# Revit family: Gira_028226
name_source: partatom
category: Electrical Fixtures
revit_build: Autodesk Revit 2017 (Build: 20160225_1515(x64)
units: mm (PartAtom-declared; Revit-internal decimal feet)

## family parameters
Cut with Voids When Loaded = No
Host = Face
Maintain Annotation Orientation = No
Part Type = Normal
Room Calculation Point = No
Round Connector Dimension = Use Diameter
Shared = No

## types (1)
- Adapter fr. square 50 x 50 mm System 55 c.alum.
    Available = No
    BIM (1) = https://media.stage.bim.site
    Category = Transition adapter for domestic switching devices
    Data sheet (1) = https://katalog.gira.de
    Default Elevation = 1219 mm
    Description = Adap.fr.square 50x50mm Sys55 CAl,Adapter frame with square cut-out for devices with cover (50 x 50 mm),,colour aluminium,Features:,- Devices with a square central plate (50 x 50 mm) from other manufacturers, e. g. Alcatel, AMP Econo Link System, Brand-Rex, BTR, Cellpack ITT Cannon Cat. 5, Deutsche Telekom, Drahtex, Hirose, Kannegieter BICC Brand Rex, Kerpen ELine 600, Krone, Molex, Nedap, Panduit, Quante, Reichle de Massari, Rutenbeck, Schumann Netzwerktechnik, HomeWay, Siemens ICCS 100, 300 and 600, Telegärtner, Telenorma, TKM (4 x RJ45 shielded, Cat. 5) can be integrated into the design line with the adapter frame and cover frame (1-gang to 5-gang).
    Dimensions = SQ50 / SQ50
    GTIN = 4010337282266
    HAN = 028226
    HeinzeBIM = https://bimportal.heinze.de
    Manufacturer = Gira
    Manufacturer URL = https://www.gira.de
    Name = Adapter fr. square 50 x 50 mm System 55 c.alum.
    URL = http://katalog.gira.de

## geometry (parser evidence)
native form markers: Blend x2, Sweep x3
no freeform markers — native parametric forms only
